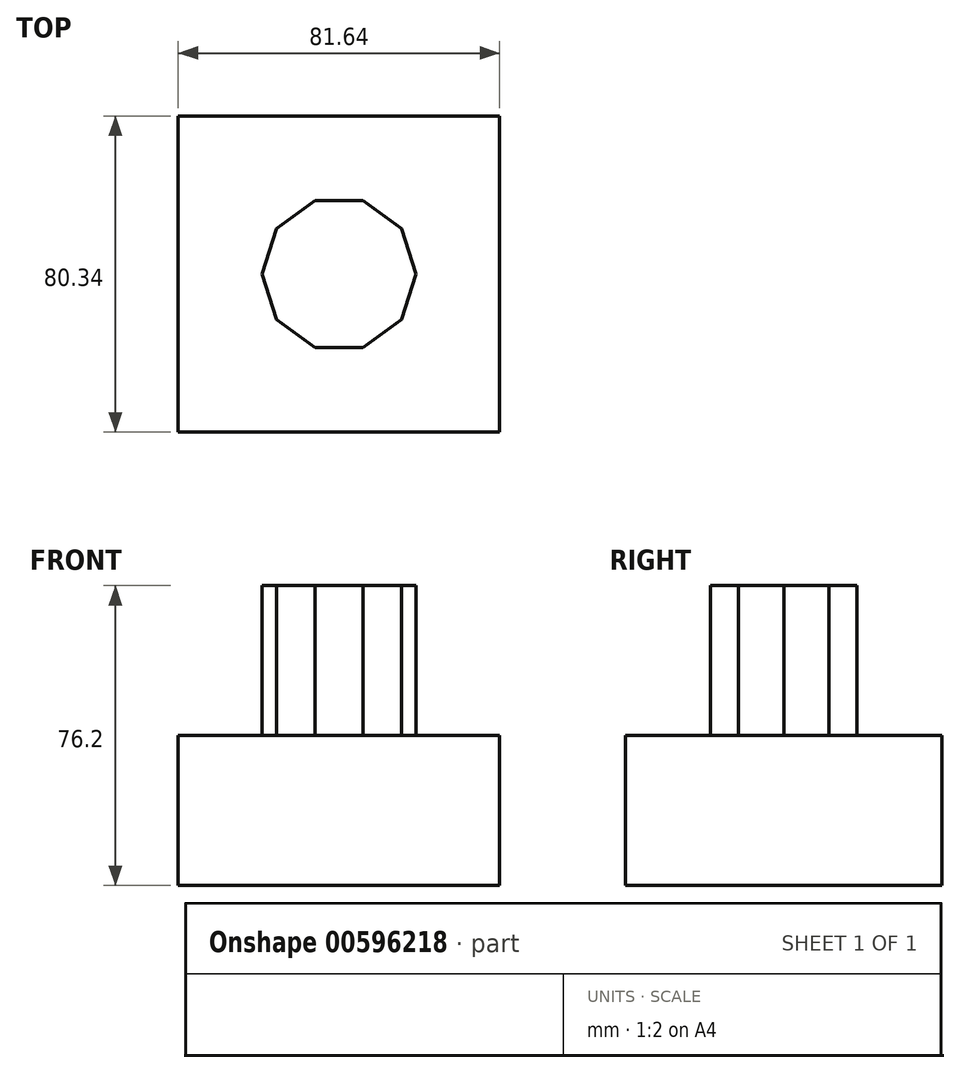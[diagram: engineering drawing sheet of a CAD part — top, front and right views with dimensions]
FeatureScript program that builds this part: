
annotation { "Feature Type Name" : "Feature", "Feature Type Description" : "" }
export const myFeature = defineFeature(function(context is Context, id is Id, definition is map)
    precondition{}
    {
        {
            var Q0;
            Q0=qCreatedBy(makeId("Top.planeOp"),FACE);
            var sketch = newSketch(context, id + "F0", { "sketchPlane" : qUnion([Q0])});
            skLineSegment(sketch, "E0.bottom", {"start": v(-40.82, 40.17) * mm, "end": v(40.82, 40.17) * mm});
            skLineSegment(sketch, "E0.top", {"start": v(-40.82, -40.17) * mm, "end": v(40.82, -40.17) * mm});
            skLineSegment(sketch, "E0.left", {"start": v(-40.82, 40.17) * mm, "end": v(-40.82, -40.17) * mm});
            skLineSegment(sketch, "E0.right", {"start": v(40.82, 40.17) * mm, "end": v(40.82, -40.17) * mm});
            skArc(sketch, "E1", {"start": v(-40.82, 40.17) * mm, "mid": v(-81, 0) * mm, "end": v(-40.82, -40.17) * mm});
            skArc(sketch, "E2", {"start": v(40.82, 40.17) * mm, "mid": v(0, 81) * mm, "end": v(-40.82, 40.17) * mm});
            skArc(sketch, "E3", {"start": v(40.82, -40.17) * mm, "mid": v(81, 0) * mm, "end": v(40.82, 40.17) * mm});
            skCircle(sketch, "E4.cCircle", {"center": v(0, 0) * mm, "radius": 18.64 * mm, "construction": true});
            skLineSegment(sketch, "E4.0", {"start": v(-6.06, 18.64) * mm, "end": v(6.06, 18.64) * mm});
            skLineSegment(sketch, "E4.1", {"start": v(6.06, 18.64) * mm, "end": v(15.86, 11.52) * mm});
            skLineSegment(sketch, "E4.2", {"start": v(15.86, 11.52) * mm, "end": v(19.6, 0) * mm});
            skLineSegment(sketch, "E4.3", {"start": v(19.6, 0) * mm, "end": v(15.86, -11.52) * mm});
            skLineSegment(sketch, "E4.4", {"start": v(15.86, -11.52) * mm, "end": v(6.06, -18.64) * mm});
            skLineSegment(sketch, "E4.5", {"start": v(6.06, -18.64) * mm, "end": v(-6.06, -18.64) * mm});
            skLineSegment(sketch, "E4.6", {"start": v(-6.06, -18.64) * mm, "end": v(-15.86, -11.52) * mm});
            skLineSegment(sketch, "E4.7", {"start": v(-15.86, -11.52) * mm, "end": v(-19.6, 0) * mm});
            skLineSegment(sketch, "E4.8", {"start": v(-19.6, 0) * mm, "end": v(-15.86, 11.52) * mm});
            skLineSegment(sketch, "E4.9", {"start": v(-15.86, 11.52) * mm, "end": v(-6.06, 18.64) * mm});
            skPoint(sketch, "E4.0.midPoint", {"position": v(0, 18.64) * mm});
            skSolve(sketch);
        }
        {
            var Q0;
            Q0=makeQuery(id+"F0.imprint","IMPRINT",FACE,{"disambiguationData":[TD([[makeQuery(id+"F0.imprint","IMPRINT",EDGE,{"derivedFrom":sQuery(id+"F0.wireOp",EDGE,"E0.bottom")}),-1.0]])]});
            extrude(context, id + "F1", {"entities" : qUnion([Q0]), "depth" : 38.1 * mm, "offsetDistance" : 25.4 * mm});
        }
        {
            var Q0;
            Q0=sQuery(id+"F0.wireOp",EDGE,"E2");
            var Q1;
            Q1=sQuery(id+"F0.wireOp",EDGE,"E1");
            var Q2;
            Q2=sQuery(id+"F0.wireOp",EDGE,"E3");
            extrude(context, id + "F2", {"bodyType" : ToolBodyType.SURFACE, "surfaceEntities" : qUnion([Q0, Q1, Q2]), "depth" : 38.1 * mm, "offsetDistance" : 25.4 * mm});
        }
        {
            var Q0;
            Q0=makeQuery(id+"F0.imprint","IMPRINT",FACE,{"disambiguationData":[TD([[makeQuery(id+"F0.imprint","IMPRINT",EDGE,{"derivedFrom":sQuery(id+"F0.wireOp",EDGE,"E4.0")}),-1.0]])]});
            extrude(context, id + "F3", {"entities" : qUnion([Q0]), "operationType" : NewBodyOperationType.ADD, "depth" : 76.2 * mm, "offsetDistance" : 25.4 * mm});
        }
    });
